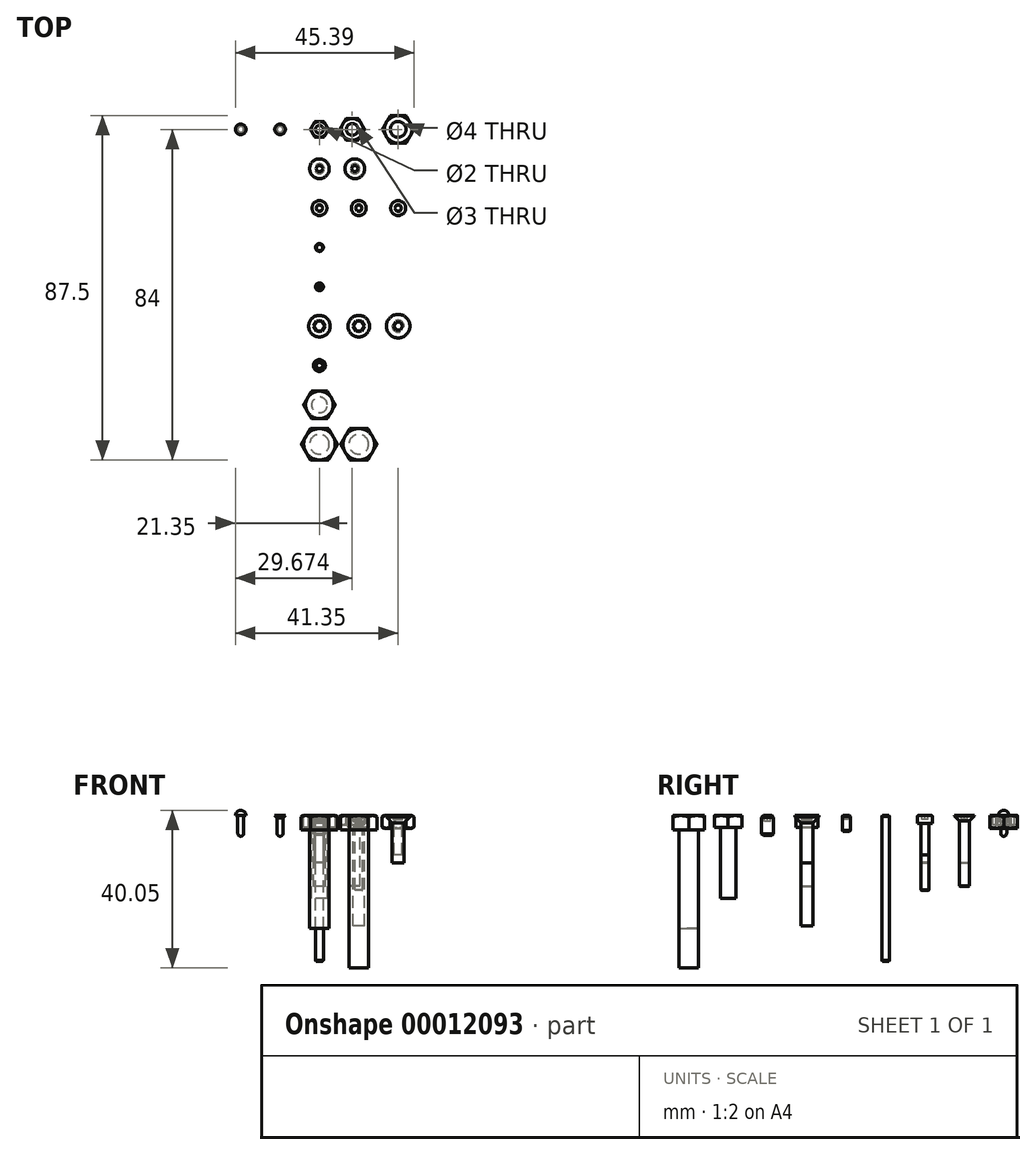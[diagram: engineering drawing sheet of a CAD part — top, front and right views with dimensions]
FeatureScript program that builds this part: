
annotation { "Feature Type Name" : "Feature", "Feature Type Description" : "" }
export const myFeature = defineFeature(function(context is Context, id is Id, definition is map)
    precondition{}
    {
        {
            var Q0;
            Q0=qCreatedBy(makeId("Top.planeOp"),FACE);
            var sketch = newSketch(context, id + "F0", { "sketchPlane" : qUnion([Q0])});
            skCircle(sketch, "E0.cCircle", {"center": v(0, 0) * mm, "radius": 2 * mm, "construction": true});
            skLineSegment(sketch, "E0.0", {"start": v(1.15, -2) * mm, "end": v(-1.15, -2) * mm});
            skLineSegment(sketch, "E0.1", {"start": v(-1.15, -2) * mm, "end": v(-2.3, 0) * mm});
            skLineSegment(sketch, "E0.2", {"start": v(-2.3, 0) * mm, "end": v(-1.15, 2) * mm});
            skLineSegment(sketch, "E0.3", {"start": v(-1.15, 2) * mm, "end": v(1.15, 2) * mm});
            skLineSegment(sketch, "E0.4", {"start": v(1.15, 2) * mm, "end": v(2.3, 0) * mm});
            skLineSegment(sketch, "E0.5", {"start": v(2.3, 0) * mm, "end": v(1.15, -2) * mm});
            skPoint(sketch, "E0.0.midPoint", {"position": v(0, -2) * mm});
            skCircle(sketch, "E1", {"center": v(0, 0) * mm, "radius": 1 * mm});
            skCircle(sketch, "E2", {"center": v(0, 0) * mm, "radius": 2 * mm});
            skSolve(sketch);
        }
        {
            var Q0;
            {var subQ1=sQuery(id+"F0.wireOp",EDGE,"E0.3");var subQ3=sQuery(id+"F0.wireOp",EDGE,"E0.2");var subQ5=makeQuery(id+"F0.imprint","INTERSECT",VERTEX,{"derivedFrom":[subQ3,subQ1]});Q0=makeQuery(id+"F0.imprint","IMPRINT",FACE,{"disambiguationData":[TD([[makeQuery(id+"F0.imprint","IMPRINT",EDGE,{"disambiguationData":[TD([[subQ5,1.0]])],"derivedFrom":subQ3}),-1.0]])]});}
            var Q1;
            {var subQ1=sQuery(id+"F0.wireOp",EDGE,"E0.2");var subQ3=sQuery(id+"F0.wireOp",EDGE,"E0.1");var subQ5=makeQuery(id+"F0.imprint","INTERSECT",VERTEX,{"derivedFrom":[subQ3,subQ1]});Q1=makeQuery(id+"F0.imprint","IMPRINT",FACE,{"disambiguationData":[TD([[makeQuery(id+"F0.imprint","IMPRINT",EDGE,{"disambiguationData":[TD([[subQ5,1.0]])],"derivedFrom":subQ3}),-1.0]])]});}
            var Q2;
            Q2=makeQuery(id+"F0.imprint","IMPRINT",FACE,{"disambiguationData":[TD([[makeQuery(id+"F0.imprint","IMPRINT",EDGE,{"derivedFrom":sQuery(id+"F0.wireOp",EDGE,"E1")}),-1.0]])]});
            var Q3;
            {var subQ1=sQuery(id+"F0.wireOp",EDGE,"E0.4");var subQ3=sQuery(id+"F0.wireOp",EDGE,"E0.3");var subQ5=makeQuery(id+"F0.imprint","INTERSECT",VERTEX,{"derivedFrom":[subQ3,subQ1]});Q3=makeQuery(id+"F0.imprint","IMPRINT",FACE,{"disambiguationData":[TD([[makeQuery(id+"F0.imprint","IMPRINT",EDGE,{"disambiguationData":[TD([[subQ5,1.0]])],"derivedFrom":subQ3}),-1.0]])]});}
            var Q4;
            {var subQ1=sQuery(id+"F0.wireOp",EDGE,"E0.5");var subQ3=sQuery(id+"F0.wireOp",EDGE,"E0.4");var subQ5=makeQuery(id+"F0.imprint","INTERSECT",VERTEX,{"derivedFrom":[subQ3,subQ1]});Q4=makeQuery(id+"F0.imprint","IMPRINT",FACE,{"disambiguationData":[TD([[makeQuery(id+"F0.imprint","IMPRINT",EDGE,{"disambiguationData":[TD([[subQ5,1.0]])],"derivedFrom":subQ3}),-1.0]])]});}
            var Q5;
            {var subQ1=sQuery(id+"F0.wireOp",EDGE,"E0.5");var subQ3=sQuery(id+"F0.wireOp",EDGE,"E0.0");var subQ5=makeQuery(id+"F0.imprint","INTERSECT",VERTEX,{"derivedFrom":[subQ3,subQ1]});Q5=makeQuery(id+"F0.imprint","IMPRINT",FACE,{"disambiguationData":[TD([[makeQuery(id+"F0.imprint","IMPRINT",EDGE,{"disambiguationData":[TD([[subQ5,-1.0]])],"derivedFrom":subQ3}),-1.0]])]});}
            var Q6;
            {var subQ1=sQuery(id+"F0.wireOp",EDGE,"E0.1");var subQ3=sQuery(id+"F0.wireOp",EDGE,"E0.0");var subQ5=makeQuery(id+"F0.imprint","INTERSECT",VERTEX,{"derivedFrom":[subQ3,subQ1]});Q6=makeQuery(id+"F0.imprint","IMPRINT",FACE,{"disambiguationData":[TD([[makeQuery(id+"F0.imprint","IMPRINT",EDGE,{"disambiguationData":[TD([[subQ5,1.0]])],"derivedFrom":subQ3}),-1.0]])]});}
            extrude(context, id + "F1", {"entities" : qUnion([Q0, Q1, Q2, Q3, Q4, Q5, Q6]), "oppositeDirection" : true, "depth" : 1.6 * mm});
        }
        {
            var Q0;
            Q0=qCreatedBy(makeId("Front.planeOp"),FACE);
            var sketch = newSketch(context, id + "F2", { "sketchPlane" : qUnion([Q0])});
            skLineSegment(sketch, "E3.0", {"start": v(-2, 0) * mm, "end": v(2, 0) * mm});
            skLineSegment(sketch, "E3.1", {"start": v(2.3, -1.6) * mm, "end": v(2.3, 0) * mm});
            skLineSegment(sketch, "E3.2", {"start": v(-2.3, -1.6) * mm, "end": v(-2.3, 0) * mm});
            skLineSegment(sketch, "E4", {"start": v(2, 0) * mm, "end": v(2.3, -0.18) * mm});
            skLineSegment(sketch, "E5", {"start": v(2, 0) * mm, "end": v(2.3, 0) * mm});
            skLineSegment(sketch, "E6", {"start": v(0, 0) * mm, "end": v(0, -1.88) * mm, "construction": true});
            skLineSegment(sketch, "E7", {"start": v(-2.3, -0.8) * mm, "end": v(0, -0.8) * mm, "construction": true});
            skLineSegment(sketch, "E8.0.MirrorCS", {"start": v(2, -1.6) * mm, "end": v(2.3, -1.6) * mm});
            skLineSegment(sketch, "E9.0.MirrorCS", {"start": v(2.3, 0) * mm, "end": v(2.3, -1.6) * mm});
            skLineSegment(sketch, "E10.0.MirrorCS", {"start": v(2, -1.6) * mm, "end": v(2.3, -1.42) * mm});
            skSolve(sketch);
        }
        {
            var Q0;
            {var subQ2=sQuery(id+"F2.wireOp",EDGE,"E4");Q0=makeQuery(id+"F2.imprint","IMPRINT",FACE,{"disambiguationData":[TD([[makeQuery(id+"F2.imprint","IMPRINT",EDGE,{"derivedFrom":subQ2}),1.0]])]});}
            var Q1;
            {var subQ2=sQuery(id+"F2.wireOp",EDGE,"E8.0.MirrorCS");Q1=makeQuery(id+"F2.imprint","IMPRINT",FACE,{"disambiguationData":[TD([[makeQuery(id+"F2.imprint","IMPRINT",EDGE,{"derivedFrom":subQ2}),1.0]])]});}
            var Q2;
            Q2=sQuery(id+"F2.wireOp",EDGE,"E6");
            revolve(context, id + "F3", {"operationType" : NewBodyOperationType.REMOVE, "entities" : qUnion([Q0, Q1]), "axis" : qUnion([Q2]), "revolveType" : RevolveType.FULL, "oppositeDirection" : true});
        }
        {
            var Q0;
            Q0=qCreatedBy(makeId("Top.planeOp"),FACE);
            var sketch = newSketch(context, id + "F4", { "sketchPlane" : qUnion([Q0])});
            skCircle(sketch, "E11.cCircle", {"center": v(8.32, 0) * mm, "radius": 2.75 * mm, "construction": true});
            skLineSegment(sketch, "E11.0", {"start": v(9.91, -2.75) * mm, "end": v(6.74, -2.75) * mm});
            skLineSegment(sketch, "E11.1", {"start": v(6.74, -2.75) * mm, "end": v(5.15, 0) * mm});
            skLineSegment(sketch, "E11.2", {"start": v(5.15, 0) * mm, "end": v(6.74, 2.75) * mm});
            skLineSegment(sketch, "E11.3", {"start": v(6.74, 2.75) * mm, "end": v(9.91, 2.75) * mm});
            skLineSegment(sketch, "E11.4", {"start": v(9.91, 2.75) * mm, "end": v(11.5, 0) * mm});
            skLineSegment(sketch, "E11.5", {"start": v(11.5, 0) * mm, "end": v(9.91, -2.75) * mm});
            skPoint(sketch, "E11.0.midPoint", {"position": v(8.32, -2.75) * mm});
            skCircle(sketch, "E12", {"center": v(8.32, 0) * mm, "radius": 1.5 * mm});
            skSolve(sketch);
        }
        {
            var Q0;
            Q0=makeQuery(id+"F4.imprint","IMPRINT",FACE,{"disambiguationData":[TD([[makeQuery(id+"F4.imprint","IMPRINT",EDGE,{"derivedFrom":sQuery(id+"F4.wireOp",EDGE,"E11.0")}),-1.0]])]});
            extrude(context, id + "F5", {"entities" : qUnion([Q0]), "oppositeDirection" : true, "depth" : 2.4 * mm});
        }
        {
            var Q0;
            Q0=qCreatedBy(makeId("Front.planeOp"),FACE);
            var sketch = newSketch(context, id + "F6", { "sketchPlane" : qUnion([Q0])});
            skLineSegment(sketch, "E13.0", {"start": v(5.57, 0) * mm, "end": v(11.07, 0) * mm});
            skLineSegment(sketch, "E13.1", {"start": v(5.15, -2.4) * mm, "end": v(5.15, 0) * mm});
            skLineSegment(sketch, "E13.2", {"start": v(11.5, -2.4) * mm, "end": v(11.5, 0) * mm});
            skLineSegment(sketch, "E14", {"start": v(5.57, 0) * mm, "end": v(5.15, -0.25) * mm});
            skLineSegment(sketch, "E15", {"start": v(5.57, 0) * mm, "end": v(5.15, 0) * mm});
            skLineSegment(sketch, "E16", {"start": v(8.32, 0) * mm, "end": v(8.32, -2.47) * mm, "construction": true});
            skLineSegment(sketch, "E17", {"start": v(11.5, -1.2) * mm, "end": v(8.32, -1.2) * mm, "construction": true});
            skLineSegment(sketch, "E18.0.MirrorCS", {"start": v(5.57, -2.4) * mm, "end": v(5.15, -2.15) * mm});
            skLineSegment(sketch, "E19.0.MirrorCS", {"start": v(5.15, 0) * mm, "end": v(5.15, -2.4) * mm});
            skLineSegment(sketch, "E20.0.MirrorCS", {"start": v(5.57, -2.4) * mm, "end": v(5.15, -2.4) * mm});
            skSolve(sketch);
        }
        {
            var Q0;
            {var subQ2=sQuery(id+"F6.wireOp",EDGE,"E14");Q0=makeQuery(id+"F6.imprint","IMPRINT",FACE,{"disambiguationData":[TD([[makeQuery(id+"F6.imprint","IMPRINT",EDGE,{"derivedFrom":subQ2}),-1.0]])]});}
            var Q1;
            {var subQ2=sQuery(id+"F6.wireOp",EDGE,"E18.0.MirrorCS");Q1=makeQuery(id+"F6.imprint","IMPRINT",FACE,{"disambiguationData":[TD([[makeQuery(id+"F6.imprint","IMPRINT",EDGE,{"derivedFrom":subQ2}),1.0]])]});}
            var Q2;
            Q2=sQuery(id+"F6.wireOp",EDGE,"E16");
            revolve(context, id + "F7", {"operationType" : NewBodyOperationType.REMOVE, "entities" : qUnion([Q0, Q1]), "axis" : qUnion([Q2]), "revolveType" : RevolveType.FULL, "oppositeDirection" : true});
        }
        {
            var Q0;
            Q0=qCreatedBy(makeId("Top.planeOp"),FACE);
            var sketch = newSketch(context, id + "F8", { "sketchPlane" : qUnion([Q0])});
            skCircle(sketch, "E21", {"center": v(17, 0) * mm, "radius": 2.5 * mm});
            skCircle(sketch, "E22", {"center": v(17, 0) * mm, "radius": 1.25 * mm});
            skCircle(sketch, "E23.cCircle", {"center": v(17, 0) * mm, "radius": 0.75 * mm, "construction": true});
            skLineSegment(sketch, "E23.0", {"start": v(17.43, -0.75) * mm, "end": v(16.57, -0.75) * mm});
            skLineSegment(sketch, "E23.1", {"start": v(16.57, -0.75) * mm, "end": v(16.13, 0) * mm});
            skLineSegment(sketch, "E23.2", {"start": v(16.13, 0) * mm, "end": v(16.57, 0.75) * mm});
            skLineSegment(sketch, "E23.3", {"start": v(16.57, 0.75) * mm, "end": v(17.43, 0.75) * mm});
            skLineSegment(sketch, "E23.4", {"start": v(17.43, 0.75) * mm, "end": v(17.87, 0) * mm});
            skLineSegment(sketch, "E23.5", {"start": v(17.87, 0) * mm, "end": v(17.43, -0.75) * mm});
            skPoint(sketch, "E23.0.midPoint", {"position": v(17, -0.75) * mm});
            skSolve(sketch);
        }
        {
            var Q0;
            Q0=makeQuery(id+"F8.imprint","IMPRINT",FACE,{"disambiguationData":[TD([[makeQuery(id+"F8.imprint","IMPRINT",EDGE,{"derivedFrom":sQuery(id+"F8.wireOp",EDGE,"E22")}),1.0]])]});
            var Q1;
            Q1=makeQuery(id+"F8.imprint","IMPRINT",FACE,{"disambiguationData":[TD([[makeQuery(id+"F8.imprint","IMPRINT",EDGE,{"derivedFrom":sQuery(id+"F8.wireOp",EDGE,"E23.0")}),-1.0]])]});
            extrude(context, id + "F9", {"entities" : qUnion([Q0, Q1]), "oppositeDirection" : true, "depth" : 15 * mm});
        }
        {
            var Q0;
            Q0=makeQuery(id+"F8.imprint","IMPRINT",FACE,{"disambiguationData":[TD([[makeQuery(id+"F8.imprint","IMPRINT",EDGE,{"derivedFrom":sQuery(id+"F8.wireOp",EDGE,"E21")}),1.0]])]});
            extrude(context, id + "F10", {"entities" : qUnion([Q0]), "operationType" : NewBodyOperationType.ADD, "oppositeDirection" : true, "depth" : 1.5 * mm});
        }
        {
            var Q0;
            Q0=makeQuery(id+"F10.opExtrude","CAP_EDGE",EDGE,{"disambiguationData":[OSD([sQuery(id+"F8.wireOp",EDGE,"E21")])],"isStart":false});
            chamfer(context, id + "F11", {"entities" : qUnion([Q0]), "width" : 1.4 * mm, "tangentPropagation" : true});
        }
        {
            var Q0;
            Q0=makeQuery(id+"F8.imprint","IMPRINT",FACE,{"disambiguationData":[TD([[makeQuery(id+"F8.imprint","IMPRINT",EDGE,{"derivedFrom":sQuery(id+"F8.wireOp",EDGE,"E23.0")}),-1.0]])]});
            extrude(context, id + "F12", {"entities" : qUnion([Q0]), "operationType" : NewBodyOperationType.REMOVE, "oppositeDirection" : true, "depth" : 1 * mm});
        }
        {
            var Q0;
            Q0=makeQuery(id+"F9.opExtrude","SWEPT_BODY",BODY,{"disambiguationData":[OSD([sQuery(id+"F8.wireOp",EDGE,"E22")])]});
            transform(context, id + "F13", {"entities" : qUnion([Q0]), "transformType" : TransformType.TRANSLATION_3D, "dx" : 10 * mm, "dy" : 0 * mm, "dz" : 0 * mm, "makeCopy" : true});
        }
        {
            var Q0;
            Q0=makeQuery(id+"F13.opPattern","COPY",FACE,{"derivedFrom":makeQuery(id+"F9.opExtrude","CAP_FACE",FACE,{"disambiguationData":[OSD([sQuery(id+"F8.wireOp",EDGE,"E22")])],"isStart":false}),"instanceName":"1"});
            extrude(context, id + "F14", {"entities" : qUnion([Q0]), "operationType" : NewBodyOperationType.ADD, "depth" : 3 * mm});
        }
        {
            var Q0;
            Q0=makeQuery(id+"F9.opExtrude","SWEPT_BODY",BODY,{"disambiguationData":[OSD([sQuery(id+"F8.wireOp",EDGE,"E22")])]});
            transform(context, id + "F15", {"entities" : qUnion([Q0]), "transformType" : TransformType.TRANSLATION_3D, "dx" : -(17 * mm), "dy" : -(10 * mm), "dz" : 0 * mm, "makeCopy" : false});
        }
        {
            var Q0;
            Q0=makeQuery(id+"F13.opPattern","COPY",BODY,{"derivedFrom":makeQuery(id+"F9.opExtrude","SWEPT_BODY",BODY,{"disambiguationData":[OSD([sQuery(id+"F8.wireOp",EDGE,"E22")])]}),"instanceName":"1"});
            transform(context, id + "F16", {"entities" : qUnion([Q0]), "transformType" : TransformType.TRANSLATION_3D, "dx" : -(18 * mm), "dy" : -10 * mm, "dz" : 0 * mm, "makeCopy" : false});
        }
        {
            var Q0;
            Q0=qCreatedBy(makeId("Top.planeOp"),FACE);
            var sketch = newSketch(context, id + "F17", { "sketchPlane" : qUnion([Q0])});
            skCircle(sketch, "E24", {"center": v(0, -20) * mm, "radius": 1.9 * mm});
            skCircle(sketch, "E25", {"center": v(0, -20) * mm, "radius": 1 * mm});
            skCircle(sketch, "E26.cCircle", {"center": v(0, -20) * mm, "radius": 0.75 * mm, "construction": true});
            skLineSegment(sketch, "E26.0", {"start": v(0.43, -20.75) * mm, "end": v(-0.43, -20.75) * mm});
            skLineSegment(sketch, "E26.1", {"start": v(-0.43, -20.75) * mm, "end": v(-0.87, -20) * mm});
            skLineSegment(sketch, "E26.2", {"start": v(-0.87, -20) * mm, "end": v(-0.43, -19.25) * mm});
            skLineSegment(sketch, "E26.3", {"start": v(-0.43, -19.25) * mm, "end": v(0.43, -19.25) * mm});
            skLineSegment(sketch, "E26.4", {"start": v(0.43, -19.25) * mm, "end": v(0.87, -20) * mm});
            skLineSegment(sketch, "E26.5", {"start": v(0.87, -20) * mm, "end": v(0.43, -20.75) * mm});
            skPoint(sketch, "E26.0.midPoint", {"position": v(0, -20.75) * mm});
            skSolve(sketch);
        }
        {
            var Q0;
            Q0=makeQuery(id+"F17.imprint","IMPRINT",FACE,{"disambiguationData":[TD([[makeQuery(id+"F17.imprint","IMPRINT",EDGE,{"derivedFrom":sQuery(id+"F17.wireOp",EDGE,"E25")}),1.0]])]});
            var Q1;
            Q1=makeQuery(id+"F17.imprint","IMPRINT",FACE,{"disambiguationData":[TD([[makeQuery(id+"F17.imprint","IMPRINT",EDGE,{"derivedFrom":sQuery(id+"F17.wireOp",EDGE,"E26.0")}),-1.0]])]});
            extrude(context, id + "F18", {"entities" : qUnion([Q0, Q1]), "oppositeDirection" : true, "depth" : 12 * mm});
        }
        {
            var Q0;
            Q0=makeQuery(id+"F17.imprint","IMPRINT",FACE,{"disambiguationData":[TD([[makeQuery(id+"F17.imprint","IMPRINT",EDGE,{"derivedFrom":sQuery(id+"F17.wireOp",EDGE,"E24")}),1.0]])]});
            extrude(context, id + "F19", {"entities" : qUnion([Q0]), "operationType" : NewBodyOperationType.ADD, "oppositeDirection" : true, "depth" : 2 * mm});
        }
        {
            var Q0;
            Q0=makeQuery(id+"F17.imprint","IMPRINT",FACE,{"disambiguationData":[TD([[makeQuery(id+"F17.imprint","IMPRINT",EDGE,{"derivedFrom":sQuery(id+"F17.wireOp",EDGE,"E26.0")}),-1.0]])]});
            extrude(context, id + "F20", {"entities" : qUnion([Q0]), "operationType" : NewBodyOperationType.REMOVE, "oppositeDirection" : true, "depth" : 1 * mm});
        }
        {
            var Q0;
            Q0=makeQuery(id+"F19.opExtrude","CAP_EDGE",EDGE,{"disambiguationData":[OSD([sQuery(id+"F17.wireOp",EDGE,"E24")])],"isStart":true});
            fillet(context, id + "F21", {"entities" : qUnion([Q0]), "radius" : 0.2 * mm, "tangentPropagation" : true, "allowEdgeOverflow" : false});
        }
        {
            var Q0;
            Q0=makeQuery(id+"F18.opExtrude","SWEPT_BODY",BODY,{"disambiguationData":[OSD([sQuery(id+"F17.wireOp",EDGE,"E25")])]});
            transform(context, id + "F22", {"entities" : qUnion([Q0]), "transformType" : TransformType.TRANSLATION_3D, "dx" : 10 * mm, "dy" : 0 * mm, "dz" : 0 * mm, "makeCopy" : true});
        }
        {
            var Q0;
            Q0=makeQuery(id+"F22.opPattern","COPY",FACE,{"derivedFrom":makeQuery(id+"F18.opExtrude","CAP_FACE",FACE,{"disambiguationData":[OSD([sQuery(id+"F17.wireOp",EDGE,"E25")])],"isStart":false}),"instanceName":"1"});
            extrude(context, id + "F23", {"entities" : qUnion([Q0]), "operationType" : NewBodyOperationType.ADD, "depth" : 7 * mm});
        }
        {
            var Q0;
            Q0=qCreatedBy(makeId("Top.planeOp"),FACE);
            var sketch = newSketch(context, id + "F24", { "sketchPlane" : qUnion([Q0])});
            skCircle(sketch, "E27", {"center": v(0, -30) * mm, "radius": 1 * mm});
            skSolve(sketch);
        }
        {
            var Q0;
            Q0=makeQuery(id+"F24.imprint","IMPRINT",FACE,{"disambiguationData":[TD([[makeQuery(id+"F24.imprint","IMPRINT",EDGE,{"derivedFrom":sQuery(id+"F24.wireOp",EDGE,"E27")}),1.0]])]});
            extrude(context, id + "F25", {"entities" : qUnion([Q0]), "oppositeDirection" : true, "depth" : 37 * mm});
        }
        {
            var Q0;
            Q0=makeQuery(id+"F25.opExtrude","CAP_EDGE",EDGE,{"disambiguationData":[OSD([sQuery(id+"F24.wireOp",EDGE,"E27")])],"isStart":false});
            var Q1;
            Q1=makeQuery(id+"F25.opExtrude","CAP_EDGE",EDGE,{"disambiguationData":[OSD([sQuery(id+"F24.wireOp",EDGE,"E27")])],"isStart":true});
            chamfer(context, id + "F26", {"entities" : qUnion([Q0, Q1]), "width" : 0.2 * mm, "tangentPropagation" : true});
        }
        {
            var Q0;
            Q0=makeQuery(id+"F22.opPattern","COPY",BODY,{"derivedFrom":makeQuery(id+"F18.opExtrude","SWEPT_BODY",BODY,{"disambiguationData":[OSD([sQuery(id+"F17.wireOp",EDGE,"E25")])]}),"instanceName":"1"});
            transform(context, id + "F27", {"entities" : qUnion([Q0]), "transformType" : TransformType.TRANSLATION_3D, "dx" : 10 * mm, "dy" : 0 * mm, "dz" : 0 * mm, "makeCopy" : true});
        }
        {
            var Q0;
            Q0=makeQuery(id+"F27.opPattern","COPY",FACE,{"derivedFrom":makeQuery(id+"F23.opExtrude","CAP_FACE",FACE,{"disambiguationData":[OSD([sQuery(id+"F17.wireOp",EDGE,"E25")])],"isStart":false}),"instanceName":"1"});
            extrude(context, id + "F28", {"entities" : qUnion([Q0]), "operationType" : NewBodyOperationType.REMOVE, "oppositeDirection" : true, "depth" : 9 * mm});
        }
        {
            var Q0;
            Q0=qCreatedBy(makeId("Top.planeOp"),FACE);
            var sketch = newSketch(context, id + "F29", { "sketchPlane" : qUnion([Q0])});
            skCircle(sketch, "E28", {"center": v(0, -40) * mm, "radius": 1 * mm});
            skCircle(sketch, "E29.cCircle", {"center": v(0, -40) * mm, "radius": 0.45 * mm, "construction": true});
            skLineSegment(sketch, "E29.0", {"start": v(0.26, -40.45) * mm, "end": v(-0.26, -40.45) * mm});
            skLineSegment(sketch, "E29.1", {"start": v(-0.26, -40.45) * mm, "end": v(-0.52, -40) * mm});
            skLineSegment(sketch, "E29.2", {"start": v(-0.52, -40) * mm, "end": v(-0.26, -39.55) * mm});
            skLineSegment(sketch, "E29.3", {"start": v(-0.26, -39.55) * mm, "end": v(0.26, -39.55) * mm});
            skLineSegment(sketch, "E29.4", {"start": v(0.26, -39.55) * mm, "end": v(0.52, -40) * mm});
            skLineSegment(sketch, "E29.5", {"start": v(0.52, -40) * mm, "end": v(0.26, -40.45) * mm});
            skPoint(sketch, "E29.0.midPoint", {"position": v(0, -40.45) * mm});
            skSolve(sketch);
        }
        {
            var Q0;
            Q0=makeQuery(id+"F29.imprint","IMPRINT",FACE,{"disambiguationData":[TD([[makeQuery(id+"F29.imprint","IMPRINT",EDGE,{"derivedFrom":sQuery(id+"F29.wireOp",EDGE,"E28")}),1.0]])]});
            var Q1;
            Q1=makeQuery(id+"F29.imprint","IMPRINT",FACE,{"disambiguationData":[TD([[makeQuery(id+"F29.imprint","IMPRINT",EDGE,{"derivedFrom":sQuery(id+"F29.wireOp",EDGE,"E29.0")}),-1.0]])]});
            extrude(context, id + "F30", {"entities" : qUnion([Q0, Q1]), "oppositeDirection" : true, "depth" : 4 * mm});
        }
        {
            var Q0;
            Q0=makeQuery(id+"F29.imprint","IMPRINT",FACE,{"disambiguationData":[TD([[makeQuery(id+"F29.imprint","IMPRINT",EDGE,{"derivedFrom":sQuery(id+"F29.wireOp",EDGE,"E29.0")}),-1.0]])]});
            extrude(context, id + "F31", {"entities" : qUnion([Q0]), "operationType" : NewBodyOperationType.REMOVE, "oppositeDirection" : true, "depth" : 1 * mm});
        }
        {
            var Q0;
            Q0=makeQuery(id+"F30.opExtrude","CAP_EDGE",EDGE,{"disambiguationData":[OSD([sQuery(id+"F29.wireOp",EDGE,"E28")])],"isStart":true});
            var Q1;
            Q1=makeQuery(id+"F30.opExtrude","CAP_EDGE",EDGE,{"disambiguationData":[OSD([sQuery(id+"F29.wireOp",EDGE,"E28")])],"isStart":false});
            chamfer(context, id + "F32", {"entities" : qUnion([Q0, Q1]), "width" : 0.2 * mm, "tangentPropagation" : true});
        }
        {
            var Q0;
            Q0=qCreatedBy(makeId("Top.planeOp"),FACE);
            var sketch = newSketch(context, id + "F33", { "sketchPlane" : qUnion([Q0])});
            skCircle(sketch, "E30", {"center": v(0, -50) * mm, "radius": 1.5 * mm});
            skCircle(sketch, "E31", {"center": v(0, -50) * mm, "radius": 2.75 * mm});
            skCircle(sketch, "E32.cCircle", {"center": v(0, -50) * mm, "radius": 1.25 * mm, "construction": true});
            skLineSegment(sketch, "E32.0", {"start": v(0.72, -51.25) * mm, "end": v(-0.72, -51.25) * mm});
            skLineSegment(sketch, "E32.1", {"start": v(-0.72, -51.25) * mm, "end": v(-1.44, -50) * mm});
            skLineSegment(sketch, "E32.2", {"start": v(-1.44, -50) * mm, "end": v(-0.72, -48.75) * mm});
            skLineSegment(sketch, "E32.3", {"start": v(-0.72, -48.75) * mm, "end": v(0.72, -48.75) * mm});
            skLineSegment(sketch, "E32.4", {"start": v(0.72, -48.75) * mm, "end": v(1.44, -50) * mm});
            skLineSegment(sketch, "E32.5", {"start": v(1.44, -50) * mm, "end": v(0.72, -51.25) * mm});
            skPoint(sketch, "E32.0.midPoint", {"position": v(0, -51.25) * mm});
            skSolve(sketch);
        }
        {
            var Q0;
            Q0=makeQuery(id+"F33.imprint","IMPRINT",FACE,{"disambiguationData":[TD([[makeQuery(id+"F33.imprint","IMPRINT",EDGE,{"derivedFrom":sQuery(id+"F33.wireOp",EDGE,"E32.0")}),-1.0]])]});
            var Q1;
            Q1=makeQuery(id+"F33.imprint","IMPRINT",FACE,{"disambiguationData":[TD([[makeQuery(id+"F33.imprint","IMPRINT",EDGE,{"derivedFrom":sQuery(id+"F33.wireOp",EDGE,"E30")}),1.0]])]});
            extrude(context, id + "F34", {"entities" : qUnion([Q0, Q1]), "oppositeDirection" : true, "depth" : 18 * mm});
        }
        {
            var Q0;
            Q0=makeQuery(id+"F33.imprint","IMPRINT",FACE,{"disambiguationData":[TD([[makeQuery(id+"F33.imprint","IMPRINT",EDGE,{"derivedFrom":sQuery(id+"F33.wireOp",EDGE,"E30")}),-1.0]])]});
            extrude(context, id + "F35", {"entities" : qUnion([Q0]), "operationType" : NewBodyOperationType.ADD, "oppositeDirection" : true, "depth" : 3 * mm});
        }
        {
            var Q0;
            Q0=makeQuery(id+"F33.imprint","IMPRINT",FACE,{"disambiguationData":[TD([[makeQuery(id+"F33.imprint","IMPRINT",EDGE,{"derivedFrom":sQuery(id+"F33.wireOp",EDGE,"E32.0")}),-1.0]])]});
            extrude(context, id + "F36", {"entities" : qUnion([Q0]), "operationType" : NewBodyOperationType.REMOVE, "oppositeDirection" : true, "depth" : 1.5 * mm});
        }
        {
            var Q0;
            Q0=makeQuery(id+"F35.opExtrude","CAP_EDGE",EDGE,{"disambiguationData":[OSD([sQuery(id+"F33.wireOp",EDGE,"E31")])],"isStart":true});
            fillet(context, id + "F37", {"entities" : qUnion([Q0]), "radius" : 0.2 * mm, "tangentPropagation" : true, "allowEdgeOverflow" : false});
        }
        {
            var Q0;
            Q0=qCreatedBy(makeId("Top.planeOp"),FACE);
            var sketch = newSketch(context, id + "F38", { "sketchPlane" : qUnion([Q0])});
            skCircle(sketch, "E33", {"center": v(0, -60) * mm, "radius": 1.5 * mm});
            skCircle(sketch, "E34.cCircle", {"center": v(0, -60) * mm, "radius": 0.75 * mm, "construction": true});
            skLineSegment(sketch, "E34.0", {"start": v(0.43, -60.75) * mm, "end": v(-0.43, -60.75) * mm});
            skLineSegment(sketch, "E34.1", {"start": v(-0.43, -60.75) * mm, "end": v(-0.87, -60) * mm});
            skLineSegment(sketch, "E34.2", {"start": v(-0.87, -60) * mm, "end": v(-0.43, -59.25) * mm});
            skLineSegment(sketch, "E34.3", {"start": v(-0.43, -59.25) * mm, "end": v(0.43, -59.25) * mm});
            skLineSegment(sketch, "E34.4", {"start": v(0.43, -59.25) * mm, "end": v(0.87, -60) * mm});
            skLineSegment(sketch, "E34.5", {"start": v(0.87, -60) * mm, "end": v(0.43, -60.75) * mm});
            skPoint(sketch, "E34.0.midPoint", {"position": v(0, -60.75) * mm});
            skSolve(sketch);
        }
        {
            var Q0;
            Q0=makeQuery(id+"F38.imprint","IMPRINT",FACE,{"disambiguationData":[TD([[makeQuery(id+"F38.imprint","IMPRINT",EDGE,{"derivedFrom":sQuery(id+"F38.wireOp",EDGE,"E33")}),1.0]])]});
            var Q1;
            Q1=makeQuery(id+"F38.imprint","IMPRINT",FACE,{"disambiguationData":[TD([[makeQuery(id+"F38.imprint","IMPRINT",EDGE,{"derivedFrom":sQuery(id+"F38.wireOp",EDGE,"E34.0")}),-1.0]])]});
            extrude(context, id + "F39", {"entities" : qUnion([Q0, Q1]), "oppositeDirection" : true, "depth" : 5 * mm});
        }
        {
            var Q0;
            Q0=makeQuery(id+"F38.imprint","IMPRINT",FACE,{"disambiguationData":[TD([[makeQuery(id+"F38.imprint","IMPRINT",EDGE,{"derivedFrom":sQuery(id+"F38.wireOp",EDGE,"E34.0")}),-1.0]])]});
            extrude(context, id + "F40", {"entities" : qUnion([Q0]), "operationType" : NewBodyOperationType.REMOVE, "oppositeDirection" : true, "depth" : 1.5 * mm});
        }
        {
            var Q0;
            Q0=makeQuery(id+"F39.opExtrude","CAP_EDGE",EDGE,{"disambiguationData":[OSD([sQuery(id+"F38.wireOp",EDGE,"E33")])],"isStart":true});
            var Q1;
            Q1=makeQuery(id+"F39.opExtrude","CAP_EDGE",EDGE,{"disambiguationData":[OSD([sQuery(id+"F38.wireOp",EDGE,"E33")])],"isStart":false});
            chamfer(context, id + "F41", {"entities" : qUnion([Q0, Q1]), "width" : 0.4 * mm, "tangentPropagation" : true});
        }
        {
            var Q0;
            Q0=makeQuery(id+"F9.opExtrude","CAP_FACE",FACE,{"disambiguationData":[OSD([sQuery(id+"F8.wireOp",EDGE,"E22")])],"isStart":false});
            extrude(context, id + "F42", {"entities" : qUnion([Q0]), "operationType" : NewBodyOperationType.REMOVE, "oppositeDirection" : true, "depth" : 3 * mm});
        }
        {
            var Q0;
            Q0=makeQuery(id+"F18.opExtrude","CAP_EDGE",EDGE,{"disambiguationData":[OSD([sQuery(id+"F17.wireOp",EDGE,"E25")])],"isStart":false});
            var Q1;
            Q1=makeQuery(id+"F23.opExtrude","CAP_EDGE",EDGE,{"disambiguationData":[OSD([sQuery(id+"F17.wireOp",EDGE,"E25")])],"isStart":false});
            var Q2;
            Q2=makeQuery(id+"F28.boolean.opBoolean","COPY",EDGE,{"derivedFrom":makeQuery(id+"F28.opExtrude","CAP_EDGE",EDGE,{"disambiguationData":[OSD([sQuery(id+"F17.wireOp",EDGE,"E25")])],"isStart":false})});
            chamfer(context, id + "F43", {"entities" : qUnion([Q0, Q1, Q2]), "width" : 0.15 * mm, "tangentPropagation" : true});
        }
        {
            var Q0;
            Q0=makeQuery(id+"F42.boolean.opBoolean","COPY",EDGE,{"derivedFrom":makeQuery(id+"F42.opExtrude","CAP_EDGE",EDGE,{"disambiguationData":[OSD([sQuery(id+"F8.wireOp",EDGE,"E22")])],"isStart":false})});
            var Q1;
            Q1=makeQuery(id+"F14.opExtrude","CAP_EDGE",EDGE,{"disambiguationData":[OSD([sQuery(id+"F8.wireOp",EDGE,"E22")])],"isStart":false});
            chamfer(context, id + "F44", {"entities" : qUnion([Q0, Q1]), "width" : 0.2 * mm, "tangentPropagation" : true});
        }
        {
            var Q0;
            Q0=makeQuery(id+"F34.opExtrude","SWEPT_BODY",BODY,{"disambiguationData":[OSD([sQuery(id+"F33.wireOp",EDGE,"E30")])]});
            transform(context, id + "F45", {"entities" : qUnion([Q0]), "transformType" : TransformType.TRANSLATION_3D, "dx" : 10 * mm, "dy" : 0 * mm, "dz" : 0 * mm, "makeCopy" : true});
        }
        {
            var Q0;
            Q0=makeQuery(id+"F45.opPattern","COPY",FACE,{"derivedFrom":makeQuery(id+"F34.opExtrude","CAP_FACE",FACE,{"disambiguationData":[OSD([sQuery(id+"F33.wireOp",EDGE,"E30")])],"isStart":false}),"instanceName":"1"});
            extrude(context, id + "F46", {"entities" : qUnion([Q0]), "operationType" : NewBodyOperationType.ADD, "depth" : 10 * mm});
        }
        {
            var Q0;
            Q0=qCreatedBy(makeId("Top.planeOp"),FACE);
            var sketch = newSketch(context, id + "F47", { "sketchPlane" : qUnion([Q0])});
            skLineSegment(sketch, "E35", {"start": v(0, 0) * mm, "end": v(20, 0) * mm, "construction": true});
            skCircle(sketch, "E36.cCircle", {"center": v(20, 0) * mm, "radius": 3.5 * mm, "construction": true});
            skLineSegment(sketch, "E36.0", {"start": v(22.02, -3.5) * mm, "end": v(17.98, -3.5) * mm});
            skLineSegment(sketch, "E36.1", {"start": v(17.98, -3.5) * mm, "end": v(15.96, 0) * mm});
            skLineSegment(sketch, "E36.2", {"start": v(15.96, 0) * mm, "end": v(17.98, 3.5) * mm});
            skLineSegment(sketch, "E36.3", {"start": v(17.98, 3.5) * mm, "end": v(22.02, 3.5) * mm});
            skLineSegment(sketch, "E36.4", {"start": v(22.02, 3.5) * mm, "end": v(24.04, 0) * mm});
            skLineSegment(sketch, "E36.5", {"start": v(24.04, 0) * mm, "end": v(22.02, -3.5) * mm});
            skPoint(sketch, "E36.0.midPoint", {"position": v(20, -3.5) * mm});
            skCircle(sketch, "E37", {"center": v(20, 0) * mm, "radius": 2 * mm});
            skCircle(sketch, "E38", {"center": v(20, 0) * mm, "radius": 3.5 * mm});
            skSolve(sketch);
        }
        {
            var Q0;
            {var subQ1=sQuery(id+"F47.wireOp",EDGE,"E36.5");var subQ3=sQuery(id+"F47.wireOp",EDGE,"E36.0");var subQ5=makeQuery(id+"F47.imprint","INTERSECT",VERTEX,{"derivedFrom":[subQ3,subQ1]});var subQ6=sQuery(id+"F47.wireOp",EDGE,"E36.1");var subQ8=makeQuery(id+"F47.imprint","INTERSECT",VERTEX,{"derivedFrom":[subQ3,subQ6]});Q0=qUnion([makeQuery(id+"F47.imprint","IMPRINT",FACE,{"disambiguationData":[TD([[makeQuery(id+"F47.imprint","IMPRINT",EDGE,{"disambiguationData":[TD([[subQ5,-1.0]])],"derivedFrom":subQ3}),-1.0]])]}),makeQuery(id+"F47.imprint","IMPRINT",FACE,{"disambiguationData":[TD([[makeQuery(id+"F47.imprint","IMPRINT",EDGE,{"disambiguationData":[TD([[subQ8,1.0]])],"derivedFrom":subQ3}),-1.0]])]})]);}
            var Q1;
            Q1=makeQuery(id+"F47.imprint","IMPRINT",FACE,{"disambiguationData":[TD([[makeQuery(id+"F47.imprint","IMPRINT",EDGE,{"derivedFrom":sQuery(id+"F47.wireOp",EDGE,"E37")}),-1.0]])]});
            var Q2;
            {var subQ1=sQuery(id+"F47.wireOp",EDGE,"E36.5");var subQ3=sQuery(id+"F47.wireOp",EDGE,"E36.4");var subQ5=makeQuery(id+"F47.imprint","INTERSECT",VERTEX,{"derivedFrom":[subQ3,subQ1]});Q2=makeQuery(id+"F47.imprint","IMPRINT",FACE,{"disambiguationData":[TD([[makeQuery(id+"F47.imprint","IMPRINT",EDGE,{"disambiguationData":[TD([[subQ5,1.0]])],"derivedFrom":subQ3}),-1.0]])]});}
            var Q3;
            {var subQ1=sQuery(id+"F47.wireOp",EDGE,"E36.4");var subQ3=sQuery(id+"F47.wireOp",EDGE,"E36.3");var subQ5=makeQuery(id+"F47.imprint","INTERSECT",VERTEX,{"derivedFrom":[subQ3,subQ1]});Q3=makeQuery(id+"F47.imprint","IMPRINT",FACE,{"disambiguationData":[TD([[makeQuery(id+"F47.imprint","IMPRINT",EDGE,{"disambiguationData":[TD([[subQ5,1.0]])],"derivedFrom":subQ3}),-1.0]])]});}
            var Q4;
            {var subQ1=sQuery(id+"F47.wireOp",EDGE,"E36.3");var subQ3=sQuery(id+"F47.wireOp",EDGE,"E36.2");var subQ5=makeQuery(id+"F47.imprint","INTERSECT",VERTEX,{"derivedFrom":[subQ3,subQ1]});Q4=makeQuery(id+"F47.imprint","IMPRINT",FACE,{"disambiguationData":[TD([[makeQuery(id+"F47.imprint","IMPRINT",EDGE,{"disambiguationData":[TD([[subQ5,1.0]])],"derivedFrom":subQ3}),-1.0]])]});}
            var Q5;
            {var subQ1=sQuery(id+"F47.wireOp",EDGE,"E36.2");var subQ3=sQuery(id+"F47.wireOp",EDGE,"E36.1");var subQ5=makeQuery(id+"F47.imprint","INTERSECT",VERTEX,{"derivedFrom":[subQ3,subQ1]});Q5=makeQuery(id+"F47.imprint","IMPRINT",FACE,{"disambiguationData":[TD([[makeQuery(id+"F47.imprint","IMPRINT",EDGE,{"disambiguationData":[TD([[subQ5,1.0]])],"derivedFrom":subQ3}),-1.0]])]});}
            extrude(context, id + "F48", {"entities" : qUnion([Q0, Q1, Q2, Q3, Q4, Q5]), "oppositeDirection" : true, "depth" : 3.2 * mm});
        }
        {
            var Q0;
            Q0=qCreatedBy(makeId("Front.planeOp"),FACE);
            var sketch = newSketch(context, id + "F49", { "sketchPlane" : qUnion([Q0])});
            skLineSegment(sketch, "E39.0", {"start": v(15.96, -3.2) * mm, "end": v(15.96, 0) * mm, "construction": true});
            skLineSegment(sketch, "E39.1", {"start": v(24.04, -3.2) * mm, "end": v(24.04, 0) * mm});
            skLineSegment(sketch, "E39.2", {"start": v(16.5, 0) * mm, "end": v(23.5, 0) * mm});
            skLineSegment(sketch, "E39.3", {"start": v(15.96, 0) * mm, "end": v(17.98, 0) * mm});
            skLineSegment(sketch, "E39.4", {"start": v(17.98, 0) * mm, "end": v(22.02, 0) * mm});
            skLineSegment(sketch, "E39.5", {"start": v(22.02, 0) * mm, "end": v(24.04, 0) * mm});
            skLineSegment(sketch, "E40", {"start": v(20, 0) * mm, "end": v(20, -3.2) * mm, "construction": true});
            skLineSegment(sketch, "E41", {"start": v(24.04, -1.6) * mm, "end": v(20, -1.6) * mm, "construction": true});
            skLineSegment(sketch, "E42", {"start": v(23.5, 0) * mm, "end": v(24.04, -0.31) * mm});
            skLineSegment(sketch, "E43.0.MirrorCS", {"start": v(23.5, -3.2) * mm, "end": v(24.04, -2.89) * mm});
            skLineSegment(sketch, "E44.0.MirrorCS", {"start": v(24.04, 0) * mm, "end": v(24.04, -3.2) * mm});
            skLineSegment(sketch, "E45", {"start": v(24.04, -3.2) * mm, "end": v(23.5, -3.2) * mm});
            skSolve(sketch);
        }
        {
            var Q0;
            {var subQ2=sQuery(id+"F49.wireOp",EDGE,"E43.0.MirrorCS");Q0=makeQuery(id+"F49.imprint","IMPRINT",FACE,{"disambiguationData":[TD([[makeQuery(id+"F49.imprint","IMPRINT",EDGE,{"derivedFrom":subQ2}),-1.0]])]});}
            var Q1;
            {var subQ1=sQuery(id+"F49.wireOp",EDGE,"E42");Q1=makeQuery(id+"F49.imprint","IMPRINT",FACE,{"disambiguationData":[TD([[makeQuery(id+"F49.imprint","IMPRINT",EDGE,{"derivedFrom":subQ1}),1.0]])]});}
            var Q2;
            Q2=sQuery(id+"F49.wireOp",EDGE,"E40");
            revolve(context, id + "F50", {"operationType" : NewBodyOperationType.REMOVE, "entities" : qUnion([Q0, Q1]), "axis" : qUnion([Q2]), "revolveType" : RevolveType.FULL, "oppositeDirection" : true});
        }
        {
            var Q0;
            Q0=qCreatedBy(makeId("Top.planeOp"),FACE);
            var sketch = newSketch(context, id + "F51", { "sketchPlane" : qUnion([Q0])});
            skLineSegment(sketch, "E46", {"start": v(0, 0) * mm, "end": v(0, -70) * mm, "construction": true});
            skCircle(sketch, "E47", {"center": v(0, -70) * mm, "radius": 2 * mm});
            skCircle(sketch, "E48", {"center": v(0, -70) * mm, "radius": 3.5 * mm});
            skCircle(sketch, "E49.cCircle", {"center": v(0, -70) * mm, "radius": 3.5 * mm, "construction": true});
            skLineSegment(sketch, "E49.0", {"start": v(2.02, -73.5) * mm, "end": v(-2.02, -73.5) * mm});
            skLineSegment(sketch, "E49.1", {"start": v(-2.02, -73.5) * mm, "end": v(-4.04, -70) * mm});
            skLineSegment(sketch, "E49.2", {"start": v(-4.04, -70) * mm, "end": v(-2.02, -66.5) * mm});
            skLineSegment(sketch, "E49.3", {"start": v(-2.02, -66.5) * mm, "end": v(2.02, -66.5) * mm});
            skLineSegment(sketch, "E49.4", {"start": v(2.02, -66.5) * mm, "end": v(4.04, -70) * mm});
            skLineSegment(sketch, "E49.5", {"start": v(4.04, -70) * mm, "end": v(2.02, -73.5) * mm});
            skPoint(sketch, "E49.0.midPoint", {"position": v(0, -73.5) * mm});
            skSolve(sketch);
        }
        {
            var Q0;
            Q0=makeQuery(id+"F51.imprint","IMPRINT",FACE,{"disambiguationData":[TD([[makeQuery(id+"F51.imprint","IMPRINT",EDGE,{"derivedFrom":sQuery(id+"F51.wireOp",EDGE,"E47")}),1.0]])]});
            extrude(context, id + "F52", {"entities" : qUnion([Q0]), "oppositeDirection" : true, "depth" : (18 + 3) * mm});
        }
        {
            var Q0;
            Q0=makeQuery(id+"F51.imprint","IMPRINT",FACE,{"disambiguationData":[TD([[makeQuery(id+"F51.imprint","IMPRINT",EDGE,{"derivedFrom":sQuery(id+"F51.wireOp",EDGE,"E47")}),-1.0]])]});
            var Q1;
            {var subQ0=sQuery(id+"F51.wireOp",EDGE,"E49.2");var subQ1=sQuery(id+"F51.wireOp",EDGE,"E48");var subQ2=makeQuery(id+"F51.imprint","INTERSECT",VERTEX,{"derivedFrom":[subQ1,subQ0]});Q1=makeQuery(id+"F51.imprint","IMPRINT",FACE,{"disambiguationData":[TD([[makeQuery(id+"F51.imprint","IMPRINT",EDGE,{"disambiguationData":[TD([[subQ2,-1.0]])],"derivedFrom":subQ1}),-1.0]])]});}
            var Q2;
            {var subQ0=sQuery(id+"F51.wireOp",EDGE,"E49.3");var subQ1=sQuery(id+"F51.wireOp",EDGE,"E48");var subQ2=makeQuery(id+"F51.imprint","INTERSECT",VERTEX,{"derivedFrom":[subQ1,subQ0]});Q2=makeQuery(id+"F51.imprint","IMPRINT",FACE,{"disambiguationData":[TD([[makeQuery(id+"F51.imprint","IMPRINT",EDGE,{"disambiguationData":[TD([[subQ2,-1.0]])],"derivedFrom":subQ1}),-1.0]])]});}
            var Q3;
            {var subQ1=sQuery(id+"F51.wireOp",EDGE,"E48");var subQ3=sQuery(id+"F51.wireOp",EDGE,"E49.3");var subQ5=makeQuery(id+"F51.imprint","INTERSECT",VERTEX,{"derivedFrom":[subQ1,subQ3]});Q3=makeQuery(id+"F51.imprint","IMPRINT",FACE,{"disambiguationData":[TD([[makeQuery(id+"F51.imprint","IMPRINT",EDGE,{"disambiguationData":[TD([[subQ5,1.0]])],"derivedFrom":subQ1}),-1.0]])]});}
            var Q4;
            {var subQ1=sQuery(id+"F51.wireOp",EDGE,"E48");var subQ3=sQuery(id+"F51.wireOp",EDGE,"E49.4");var subQ5=makeQuery(id+"F51.imprint","INTERSECT",VERTEX,{"derivedFrom":[subQ1,subQ3]});Q4=makeQuery(id+"F51.imprint","IMPRINT",FACE,{"disambiguationData":[TD([[makeQuery(id+"F51.imprint","IMPRINT",EDGE,{"disambiguationData":[TD([[subQ5,1.0]])],"derivedFrom":subQ1}),-1.0]])]});}
            var Q5;
            {var subQ1=sQuery(id+"F51.wireOp",EDGE,"E48");var subQ3=sQuery(id+"F51.wireOp",EDGE,"E49.0");var subQ5=makeQuery(id+"F51.imprint","INTERSECT",VERTEX,{"derivedFrom":[subQ1,subQ3]});Q5=makeQuery(id+"F51.imprint","IMPRINT",FACE,{"disambiguationData":[TD([[makeQuery(id+"F51.imprint","IMPRINT",EDGE,{"disambiguationData":[TD([[subQ5,-1.0]])],"derivedFrom":subQ1}),-1.0]])]});}
            var Q6;
            {var subQ0=sQuery(id+"F51.wireOp",EDGE,"E49.1");var subQ1=sQuery(id+"F51.wireOp",EDGE,"E48");var subQ2=makeQuery(id+"F51.imprint","INTERSECT",VERTEX,{"derivedFrom":[subQ1,subQ0]});Q6=makeQuery(id+"F51.imprint","IMPRINT",FACE,{"disambiguationData":[TD([[makeQuery(id+"F51.imprint","IMPRINT",EDGE,{"disambiguationData":[TD([[subQ2,-1.0]])],"derivedFrom":subQ1}),-1.0]])]});}
            extrude(context, id + "F53", {"entities" : qUnion([Q0, Q1, Q2, Q3, Q4, Q5, Q6]), "operationType" : NewBodyOperationType.ADD, "oppositeDirection" : true, "depth" : 3 * mm});
        }
        {
            var Q0;
            Q0=qCreatedBy(makeId("Right.planeOp"),FACE);
            var sketch = newSketch(context, id + "F54", { "sketchPlane" : qUnion([Q0])});
            skLineSegment(sketch, "E50.0", {"start": v(-73.5, 0) * mm, "end": v(-66.5, 0) * mm});
            skLineSegment(sketch, "E50.1", {"start": v(-70, -3) * mm, "end": v(-66.5, -3) * mm});
            skLineSegment(sketch, "E50.2", {"start": v(-73.5, -3) * mm, "end": v(-70, -3) * mm});
            skLineSegment(sketch, "E51", {"start": v(-70, 0) * mm, "end": v(-70, -3) * mm, "construction": true});
            skLineSegment(sketch, "E52", {"start": v(-70, -1.5) * mm, "end": v(-66.5, -1.5) * mm, "construction": true});
            skLineSegment(sketch, "E53", {"start": v(-66.5, 0) * mm, "end": v(-64.6, 0) * mm});
            skLineSegment(sketch, "E54", {"start": v(-64.6, 0) * mm, "end": v(-64.6, -1.1) * mm});
            skLineSegment(sketch, "E55", {"start": v(-64.6, -1.1) * mm, "end": v(-66.5, 0) * mm});
            skLineSegment(sketch, "E56.0.MirrorCS", {"start": v(-64.6, -1.9) * mm, "end": v(-66.5, -3) * mm});
            skLineSegment(sketch, "E57.0.MirrorCS", {"start": v(-66.5, -3) * mm, "end": v(-64.6, -3) * mm});
            skLineSegment(sketch, "E58.0.MirrorCS", {"start": v(-64.6, -3) * mm, "end": v(-64.6, -1.9) * mm});
            skSolve(sketch);
        }
        {
            var Q0;
            Q0=makeQuery(id+"F54.imprint","IMPRINT",FACE,{"disambiguationData":[TD([[makeQuery(id+"F54.imprint","IMPRINT",EDGE,{"derivedFrom":sQuery(id+"F54.wireOp",EDGE,"E53")}),-1.0]])]});
            var Q1;
            Q1=sQuery(id+"F54.wireOp",EDGE,"E51");
            revolve(context, id + "F55", {"operationType" : NewBodyOperationType.REMOVE, "entities" : qUnion([Q0]), "axis" : qUnion([Q1]), "revolveType" : RevolveType.FULL, "oppositeDirection" : true});
        }
        {
            var Q0;
            Q0=qCreatedBy(makeId("Top.planeOp"),FACE);
            var sketch = newSketch(context, id + "F56", { "sketchPlane" : qUnion([Q0])});
            skCircle(sketch, "E59.0", {"center": v(0, -70) * mm, "radius": 2 * mm, "construction": true});
            skLineSegment(sketch, "E60", {"start": v(0, -70) * mm, "end": v(0, -80) * mm, "construction": true});
            skCircle(sketch, "E61", {"center": v(0, -80) * mm, "radius": 2.5 * mm});
            skCircle(sketch, "E62", {"center": v(0, -80) * mm, "radius": 4 * mm});
            skCircle(sketch, "E63.cCircle", {"center": v(0, -80) * mm, "radius": 4 * mm, "construction": true});
            skLineSegment(sketch, "E63.0", {"start": v(2.3, -84) * mm, "end": v(-2.3, -84) * mm});
            skLineSegment(sketch, "E63.1", {"start": v(-2.3, -84) * mm, "end": v(-4.62, -80) * mm});
            skLineSegment(sketch, "E63.2", {"start": v(-4.62, -80) * mm, "end": v(-2.3, -76) * mm});
            skLineSegment(sketch, "E63.3", {"start": v(-2.3, -76) * mm, "end": v(2.3, -76) * mm});
            skLineSegment(sketch, "E63.4", {"start": v(2.3, -76) * mm, "end": v(4.62, -80) * mm});
            skLineSegment(sketch, "E63.5", {"start": v(4.62, -80) * mm, "end": v(2.3, -84) * mm});
            skPoint(sketch, "E63.0.midPoint", {"position": v(0, -84) * mm});
            skSolve(sketch);
        }
        {
            var Q0;
            Q0=makeQuery(id+"F56.imprint","IMPRINT",FACE,{"disambiguationData":[TD([[makeQuery(id+"F56.imprint","IMPRINT",EDGE,{"derivedFrom":sQuery(id+"F56.wireOp",EDGE,"E61")}),1.0]])]});
            extrude(context, id + "F57", {"entities" : qUnion([Q0]), "oppositeDirection" : true, "depth" : (25 + 3.7) * mm});
        }
        {
            var Q0;
            Q0=makeQuery(id+"F56.imprint","IMPRINT",FACE,{"disambiguationData":[TD([[makeQuery(id+"F56.imprint","IMPRINT",EDGE,{"derivedFrom":sQuery(id+"F56.wireOp",EDGE,"E61")}),-1.0]])]});
            var Q1;
            {var subQ0=sQuery(id+"F56.wireOp",EDGE,"E63.3");var subQ1=sQuery(id+"F56.wireOp",EDGE,"E62");var subQ2=makeQuery(id+"F56.imprint","INTERSECT",VERTEX,{"derivedFrom":[subQ1,subQ0]});Q1=makeQuery(id+"F56.imprint","IMPRINT",FACE,{"disambiguationData":[TD([[makeQuery(id+"F56.imprint","IMPRINT",EDGE,{"disambiguationData":[TD([[subQ2,-1.0]])],"derivedFrom":subQ1}),-1.0]])]});}
            var Q2;
            {var subQ0=sQuery(id+"F56.wireOp",EDGE,"E63.3");var subQ1=sQuery(id+"F56.wireOp",EDGE,"E62");var subQ2=makeQuery(id+"F56.imprint","INTERSECT",VERTEX,{"derivedFrom":[subQ1,subQ0]});Q2=makeQuery(id+"F56.imprint","IMPRINT",FACE,{"disambiguationData":[TD([[makeQuery(id+"F56.imprint","IMPRINT",EDGE,{"disambiguationData":[TD([[subQ2,1.0]])],"derivedFrom":subQ1}),-1.0]])]});}
            var Q3;
            {var subQ0=sQuery(id+"F56.wireOp",EDGE,"E63.2");var subQ1=sQuery(id+"F56.wireOp",EDGE,"E62");var subQ2=makeQuery(id+"F56.imprint","INTERSECT",VERTEX,{"derivedFrom":[subQ1,subQ0]});Q3=makeQuery(id+"F56.imprint","IMPRINT",FACE,{"disambiguationData":[TD([[makeQuery(id+"F56.imprint","IMPRINT",EDGE,{"disambiguationData":[TD([[subQ2,-1.0]])],"derivedFrom":subQ1}),-1.0]])]});}
            var Q4;
            {var subQ0=sQuery(id+"F56.wireOp",EDGE,"E63.1");var subQ1=sQuery(id+"F56.wireOp",EDGE,"E62");var subQ2=makeQuery(id+"F56.imprint","INTERSECT",VERTEX,{"derivedFrom":[subQ1,subQ0]});Q4=makeQuery(id+"F56.imprint","IMPRINT",FACE,{"disambiguationData":[TD([[makeQuery(id+"F56.imprint","IMPRINT",EDGE,{"disambiguationData":[TD([[subQ2,-1.0]])],"derivedFrom":subQ1}),-1.0]])]});}
            var Q5;
            {var subQ1=sQuery(id+"F56.wireOp",EDGE,"E62");var subQ3=sQuery(id+"F56.wireOp",EDGE,"E63.0");var subQ5=makeQuery(id+"F56.imprint","INTERSECT",VERTEX,{"derivedFrom":[subQ1,subQ3]});Q5=makeQuery(id+"F56.imprint","IMPRINT",FACE,{"disambiguationData":[TD([[makeQuery(id+"F56.imprint","IMPRINT",EDGE,{"disambiguationData":[TD([[subQ5,-1.0]])],"derivedFrom":subQ1}),-1.0]])]});}
            var Q6;
            {var subQ1=sQuery(id+"F56.wireOp",EDGE,"E62");var subQ3=sQuery(id+"F56.wireOp",EDGE,"E63.4");var subQ5=makeQuery(id+"F56.imprint","INTERSECT",VERTEX,{"derivedFrom":[subQ1,subQ3]});Q6=makeQuery(id+"F56.imprint","IMPRINT",FACE,{"disambiguationData":[TD([[makeQuery(id+"F56.imprint","IMPRINT",EDGE,{"disambiguationData":[TD([[subQ5,1.0]])],"derivedFrom":subQ1}),-1.0]])]});}
            extrude(context, id + "F58", {"entities" : qUnion([Q0, Q1, Q2, Q3, Q4, Q5, Q6]), "operationType" : NewBodyOperationType.ADD, "oppositeDirection" : true, "depth" : 3.7 * mm});
        }
        {
            var Q0;
            Q0=qCreatedBy(makeId("Right.planeOp"),FACE);
            var sketch = newSketch(context, id + "F59", { "sketchPlane" : qUnion([Q0])});
            skLineSegment(sketch, "E64.0", {"start": v(-84, 0) * mm, "end": v(-76, 0) * mm});
            skLineSegment(sketch, "E65", {"start": v(-80, 0) * mm, "end": v(-80, -2.78) * mm, "construction": true});
            skLineSegment(sketch, "E66", {"start": v(-84, 0) * mm, "end": v(-86.4, 0) * mm});
            skLineSegment(sketch, "E67", {"start": v(-86.4, 0) * mm, "end": v(-86.4, -1.38) * mm});
            skLineSegment(sketch, "E68", {"start": v(-86.4, -1.38) * mm, "end": v(-84, 0) * mm});
            skSolve(sketch);
        }
        {
            var Q0;
            Q0=makeQuery(id+"F59.imprint","IMPRINT",FACE,{"disambiguationData":[TD([[makeQuery(id+"F59.imprint","IMPRINT",EDGE,{"derivedFrom":sQuery(id+"F59.wireOp",EDGE,"E66")}),1.0]])]});
            var Q1;
            Q1=sQuery(id+"F59.wireOp",EDGE,"E65");
            revolve(context, id + "F60", {"operationType" : NewBodyOperationType.REMOVE, "entities" : qUnion([Q0]), "axis" : qUnion([Q1]), "revolveType" : RevolveType.FULL, "oppositeDirection" : true});
        }
        {
            var Q0;
            Q0=makeQuery(id+"F57.opExtrude","SWEPT_BODY",BODY,{"disambiguationData":[OSD([sQuery(id+"F56.wireOp",EDGE,"E61")])]});
            transform(context, id + "F61", {"entities" : qUnion([Q0]), "transformType" : TransformType.TRANSLATION_3D, "dx" : 10 * mm, "dy" : 0 * mm, "dz" : 0 * mm, "makeCopy" : true});
        }
        {
            var Q0;
            Q0=makeQuery(id+"F61.opPattern","COPY",FACE,{"derivedFrom":makeQuery(id+"F57.opExtrude","CAP_FACE",FACE,{"disambiguationData":[OSD([sQuery(id+"F56.wireOp",EDGE,"E61")])],"isStart":false}),"instanceName":"1"});
            extrude(context, id + "F62", {"entities" : qUnion([Q0]), "operationType" : NewBodyOperationType.ADD, "depth" : 10 * mm});
        }
        {
            var Q0;
            Q0=qCreatedBy(makeId("Top.planeOp"),FACE);
            var sketch = newSketch(context, id + "F63", { "sketchPlane" : qUnion([Q0])});
            skLineSegment(sketch, "E69", {"start": v(0, -50) * mm, "end": v(20, -50) * mm, "construction": true});
            skCircle(sketch, "E70", {"center": v(20, -50) * mm, "radius": 1.5 * mm});
            skCircle(sketch, "E71", {"center": v(20, -50) * mm, "radius": 3 * mm});
            skCircle(sketch, "E72", {"center": v(20, -50) * mm, "radius": 3.36 * mm});
            skCircle(sketch, "E73.cCircle", {"center": v(20, -50) * mm, "radius": 1 * mm, "construction": true});
            skLineSegment(sketch, "E73.0", {"start": v(20.58, -51) * mm, "end": v(19.42, -51) * mm});
            skLineSegment(sketch, "E73.1", {"start": v(19.42, -51) * mm, "end": v(18.85, -50) * mm});
            skLineSegment(sketch, "E73.2", {"start": v(18.85, -50) * mm, "end": v(19.42, -49) * mm});
            skLineSegment(sketch, "E73.3", {"start": v(19.42, -49) * mm, "end": v(20.58, -49) * mm});
            skLineSegment(sketch, "E73.4", {"start": v(20.58, -49) * mm, "end": v(21.15, -50) * mm});
            skLineSegment(sketch, "E73.5", {"start": v(21.15, -50) * mm, "end": v(20.58, -51) * mm});
            skPoint(sketch, "E73.0.midPoint", {"position": v(20, -51) * mm});
            skSolve(sketch);
        }
        {
            var Q0;
            Q0=makeQuery(id+"F63.imprint","IMPRINT",FACE,{"disambiguationData":[TD([[makeQuery(id+"F63.imprint","IMPRINT",EDGE,{"derivedFrom":sQuery(id+"F63.wireOp",EDGE,"E70")}),1.0]])]});
            var Q1;
            Q1=makeQuery(id+"F63.imprint","IMPRINT",FACE,{"disambiguationData":[TD([[makeQuery(id+"F63.imprint","IMPRINT",EDGE,{"derivedFrom":sQuery(id+"F63.wireOp",EDGE,"E73.0")}),-1.0]])]});
            extrude(context, id + "F64", {"entities" : qUnion([Q0, Q1]), "oppositeDirection" : true, "depth" : 12 * mm});
        }
        {
            var Q0;
            Q0=makeQuery(id+"F63.imprint","IMPRINT",FACE,{"disambiguationData":[TD([[makeQuery(id+"F63.imprint","IMPRINT",EDGE,{"derivedFrom":sQuery(id+"F63.wireOp",EDGE,"E70")}),-1.0]])]});
            var Q1;
            Q1=makeQuery(id+"F63.imprint","IMPRINT",FACE,{"disambiguationData":[TD([[makeQuery(id+"F63.imprint","IMPRINT",EDGE,{"derivedFrom":sQuery(id+"F63.wireOp",EDGE,"E71")}),-1.0]])]});
            extrude(context, id + "F65", {"entities" : qUnion([Q0, Q1]), "operationType" : NewBodyOperationType.ADD, "oppositeDirection" : true, "depth" : 1.86 * mm});
        }
        {
            var Q0;
            Q0=makeQuery(id+"F65.opExtrude","CAP_EDGE",EDGE,{"disambiguationData":[OSD([sQuery(id+"F63.wireOp",EDGE,"E72")])],"isStart":false});
            chamfer(context, id + "F66", {"entities" : qUnion([Q0]), "width" : 1.85 * mm, "tangentPropagation" : true});
        }
        {
            var Q0;
            Q0=makeQuery(id+"F63.imprint","IMPRINT",FACE,{"disambiguationData":[TD([[makeQuery(id+"F63.imprint","IMPRINT",EDGE,{"derivedFrom":sQuery(id+"F63.wireOp",EDGE,"E71")}),-1.0]])]});
            extrude(context, id + "F67", {"entities" : qUnion([Q0]), "operationType" : NewBodyOperationType.REMOVE, "oppositeDirection" : true, "depth" : 1 * mm});
        }
        {
            var Q0;
            Q0=makeQuery(id+"F63.imprint","IMPRINT",FACE,{"disambiguationData":[TD([[makeQuery(id+"F63.imprint","IMPRINT",EDGE,{"derivedFrom":sQuery(id+"F63.wireOp",EDGE,"E73.0")}),-1.0]])]});
            extrude(context, id + "F68", {"entities" : qUnion([Q0]), "operationType" : NewBodyOperationType.REMOVE, "oppositeDirection" : true, "depth" : 1.05 * mm});
        }
        {
            var Q0;
            Q0=qCreatedBy(makeId("Top.planeOp"),FACE);
            var sketch = newSketch(context, id + "F69", { "sketchPlane" : qUnion([Q0])});
            skLineSegment(sketch, "E74", {"start": v(0, 0) * mm, "end": v(-10, 0) * mm, "construction": true});
            skCircle(sketch, "E75", {"center": v(-10, 0) * mm, "radius": 0.75 * mm});
            skCircle(sketch, "E76", {"center": v(-10, 0) * mm, "radius": 1.35 * mm});
            skSolve(sketch);
        }
        {
            var Q0;
            Q0=makeQuery(id+"F69.imprint","IMPRINT",FACE,{"disambiguationData":[TD([[makeQuery(id+"F69.imprint","IMPRINT",EDGE,{"derivedFrom":sQuery(id+"F69.wireOp",EDGE,"E75")}),1.0]])]});
            extrude(context, id + "F70", {"entities" : qUnion([Q0]), "oppositeDirection" : true, "depth" : 4.5 * mm});
        }
        {
            var Q0;
            Q0=makeQuery(id+"F69.imprint","IMPRINT",FACE,{"disambiguationData":[TD([[makeQuery(id+"F69.imprint","IMPRINT",EDGE,{"derivedFrom":sQuery(id+"F69.wireOp",EDGE,"E75")}),-1.0]])]});
            extrude(context, id + "F71", {"entities" : qUnion([Q0]), "operationType" : NewBodyOperationType.ADD, "oppositeDirection" : true, "depth" : 0.75 * mm});
        }
        {
            var Q0;
            Q0=makeQuery(id+"F71.opExtrude","CAP_EDGE",EDGE,{"disambiguationData":[OSD([sQuery(id+"F69.wireOp",EDGE,"E76")])],"isStart":false});
            chamfer(context, id + "F72", {"entities" : qUnion([Q0]), "width" : 0.75 * mm, "tangentPropagation" : true});
        }
        {
            var Q0;
            Q0=makeQuery(id+"F70.opExtrude","CAP_FACE",FACE,{"disambiguationData":[OSD([sQuery(id+"F69.wireOp",EDGE,"E75")])],"isStart":false});
            var sketch = newSketch(context, id + "F73", { "sketchPlane" : qUnion([Q0])});
            skCircle(sketch, "E77.0", {"center": v(-10, 0) * mm, "radius": 1.35 * mm});
            skLineSegment(sketch, "E78", {"start": v(-10, 1.35) * mm, "end": v(-10, -1.35) * mm});
            skSolve(sketch);
        }
        {
            var Q0;
            {var subQ1=sQuery(id+"F73.wireOp",EDGE,"E78");var subQ4=sQuery(id+"F73.wireOp",EDGE,"E77.0");var subQ6=makeQuery(id+"F73.imprint","INTERSECT",VERTEX,{"disambiguationData":[OD(0.0)],"derivedFrom":[subQ4,subQ1]});Q0=makeQuery(id+"F73.imprint","IMPRINT",FACE,{"disambiguationData":[TD([[makeQuery(id+"F73.imprint","IMPRINT",EDGE,{"disambiguationData":[TD([[subQ6,-1.0]])],"derivedFrom":subQ4}),-1.0]])]});}
            var Q1;
            {var subQ0=makeQuery(id+"F70.opExtrude","CAP_EDGE",EDGE,{"disambiguationData":[OSD([sQuery(id+"F69.wireOp",EDGE,"E75")])],"isStart":false});var subQ1=sQuery(id+"F73.wireOp",EDGE,"E78");var subQ3=makeQuery(id+"F73.imprint","INTERSECT",VERTEX,{"disambiguationData":[OD(0.0)],"derivedFrom":[subQ0,subQ1]});Q1=makeQuery(id+"F73.imprint","IMPRINT",FACE,{"disambiguationData":[TD([[makeQuery(id+"F73.imprint","IMPRINT",EDGE,{"disambiguationData":[TD([[subQ3,-1.0]])],"derivedFrom":subQ1}),1.0]])]});}
            var Q2;
            Q2=sQuery(id+"F73.wireOp",EDGE,"E78");
            revolve(context, id + "F74", {"operationType" : NewBodyOperationType.ADD, "entities" : qUnion([Q0, Q1]), "axis" : qUnion([Q2]), "revolveType" : RevolveType.ONE_DIRECTION, "angle" : 180 * degree});
        }
        {
            var Q0;
            Q0=qCreatedBy(makeId("Top.planeOp"),FACE);
            var sketch = newSketch(context, id + "F75", { "sketchPlane" : qUnion([Q0])});
            skLineSegment(sketch, "E79", {"start": v(0, 0) * mm, "end": v(-20, 0) * mm, "construction": true});
            skCircle(sketch, "E80", {"center": v(-20, 0) * mm, "radius": 0.75 * mm});
            skCircle(sketch, "E81", {"center": v(-20, 0) * mm, "radius": 1.35 * mm});
            skLineSegment(sketch, "E82", {"start": v(-18.65, 0) * mm, "end": v(-21.35, 0) * mm});
            skSolve(sketch);
        }
        {
            var Q0;
            {var subQ0=sQuery(id+"F75.wireOp",EDGE,"E82");var subQ1=sQuery(id+"F75.wireOp",EDGE,"E80");var subQ3=makeQuery(id+"F75.imprint","INTERSECT",VERTEX,{"disambiguationData":[OD(0.0)],"derivedFrom":[subQ1,subQ0]});Q0=makeQuery(id+"F75.imprint","IMPRINT",FACE,{"disambiguationData":[TD([[makeQuery(id+"F75.imprint","IMPRINT",EDGE,{"disambiguationData":[TD([[subQ3,-1.0]])],"derivedFrom":subQ1}),1.0]])]});}
            var Q1;
            {var subQ0=sQuery(id+"F75.wireOp",EDGE,"E82");var subQ1=sQuery(id+"F75.wireOp",EDGE,"E80");var subQ3=makeQuery(id+"F75.imprint","INTERSECT",VERTEX,{"disambiguationData":[OD(0.0)],"derivedFrom":[subQ1,subQ0]});Q1=makeQuery(id+"F75.imprint","IMPRINT",FACE,{"disambiguationData":[TD([[makeQuery(id+"F75.imprint","IMPRINT",EDGE,{"disambiguationData":[TD([[subQ3,1.0]])],"derivedFrom":subQ1}),1.0]])]});}
            extrude(context, id + "F76", {"entities" : qUnion([Q0, Q1]), "oppositeDirection" : true, "depth" : 4.5 * mm});
        }
        {
            var Q0;
            {var subQ0=sQuery(id+"F75.wireOp",EDGE,"E82");var subQ1=sQuery(id+"F75.wireOp",EDGE,"E80");var subQ5=makeQuery(id+"F75.imprint","INTERSECT",VERTEX,{"disambiguationData":[OD(0.0)],"derivedFrom":[subQ1,subQ0]});Q0=makeQuery(id+"F75.imprint","IMPRINT",FACE,{"disambiguationData":[TD([[makeQuery(id+"F75.imprint","IMPRINT",EDGE,{"disambiguationData":[TD([[subQ5,-1.0]])],"derivedFrom":subQ1}),-1.0]])]});}
            var Q1;
            {var subQ0=sQuery(id+"F75.wireOp",EDGE,"E82");var subQ1=sQuery(id+"F75.wireOp",EDGE,"E80");var subQ3=makeQuery(id+"F75.imprint","INTERSECT",VERTEX,{"disambiguationData":[OD(0.0)],"derivedFrom":[subQ1,subQ0]});Q1=makeQuery(id+"F75.imprint","IMPRINT",FACE,{"disambiguationData":[TD([[makeQuery(id+"F75.imprint","IMPRINT",EDGE,{"disambiguationData":[TD([[subQ3,-1.0]])],"derivedFrom":subQ1}),1.0]])]});}
            var Q2;
            Q2=sQuery(id+"F75.wireOp",EDGE,"E82");
            revolve(context, id + "F77", {"operationType" : NewBodyOperationType.ADD, "entities" : qUnion([Q0, Q1]), "axis" : qUnion([Q2]), "revolveType" : RevolveType.ONE_DIRECTION, "oppositeDirection" : true, "angle" : 180 * degree});
        }
        {
            var Q0;
            Q0=makeQuery(id+"F76.opExtrude","CAP_FACE",FACE,{"disambiguationData":[OSD([sQuery(id+"F75.wireOp",EDGE,"E80")])],"isStart":false});
            var sketch = newSketch(context, id + "F78", { "sketchPlane" : qUnion([Q0])});
            skCircle(sketch, "E83.0", {"center": v(-20, 0) * mm, "radius": 1.35 * mm});
            skLineSegment(sketch, "E83.1", {"start": v(-18.65, 0) * mm, "end": v(-21.35, 0) * mm});
            skSolve(sketch);
        }
        {
            var Q0;
            {var subQ1=sQuery(id+"F78.wireOp",EDGE,"E83.1");var subQ4=sQuery(id+"F78.wireOp",EDGE,"E83.0");var subQ6=makeQuery(id+"F78.imprint","INTERSECT",VERTEX,{"disambiguationData":[OD(0.0)],"derivedFrom":[subQ4,subQ1]});Q0=makeQuery(id+"F78.imprint","IMPRINT",FACE,{"disambiguationData":[TD([[makeQuery(id+"F78.imprint","IMPRINT",EDGE,{"disambiguationData":[TD([[subQ6,1.0]])],"derivedFrom":subQ4}),-1.0]])]});}
            var Q1;
            {var subQ0=makeQuery(id+"F76.opExtrude","CAP_EDGE",EDGE,{"disambiguationData":[OSD([sQuery(id+"F75.wireOp",EDGE,"E80")])],"isStart":false});var subQ1=sQuery(id+"F78.wireOp",EDGE,"E83.1");var subQ3=makeQuery(id+"F78.imprint","INTERSECT",VERTEX,{"disambiguationData":[OD(0.0)],"derivedFrom":[subQ0,subQ1]});Q1=makeQuery(id+"F78.imprint","IMPRINT",FACE,{"disambiguationData":[TD([[makeQuery(id+"F78.imprint","IMPRINT",EDGE,{"disambiguationData":[TD([[subQ3,-1.0]])],"derivedFrom":subQ1}),-1.0]])]});}
            var Q2;
            Q2=sQuery(id+"F78.wireOp",EDGE,"E83.1");
            revolve(context, id + "F79", {"operationType" : NewBodyOperationType.ADD, "entities" : qUnion([Q0, Q1]), "axis" : qUnion([Q2]), "revolveType" : RevolveType.ONE_DIRECTION, "oppositeDirection" : true, "angle" : 180 * degree});
        }
    });
